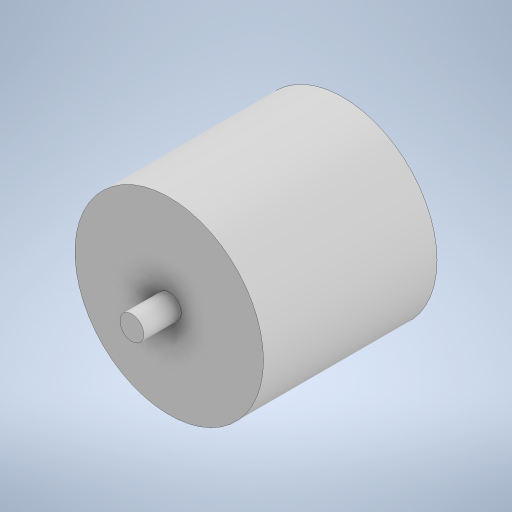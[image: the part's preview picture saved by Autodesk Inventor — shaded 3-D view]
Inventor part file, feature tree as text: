
AUTODESK INVENTOR PART (.ipt)
format: ipt  version: 2023 (Build 270158000, 158)  size: 217,600 bytes
history: native  units: in
note: dims shown in document units (in); Inventor stores cm internally (conversion verified against a paired STEP export)
features: sketch x3, extrude x2
ambient origin geometry x8: Origin, YZ Plane, XZ Plane, XY Plane, X Axis, Y Axis, Z Axis, Center Point
bodies: Solid1 (feature_tree)
feature tree (5):
  extrude  "Extrusion1"  Depth=3.2677in TaperAngle=0.0deg
  extrude  "Extrusion2"  Depth=2.2835in TaperAngle=0.0deg
  sketch  "Sketch4"
  sketch  "Sketch2"  dims[d0=0.315in d1=3.2677in d2=0.0in]
  sketch  "Sketch3"  dims[d3=2.4803in d4=2.2835in d5=0.0in]
